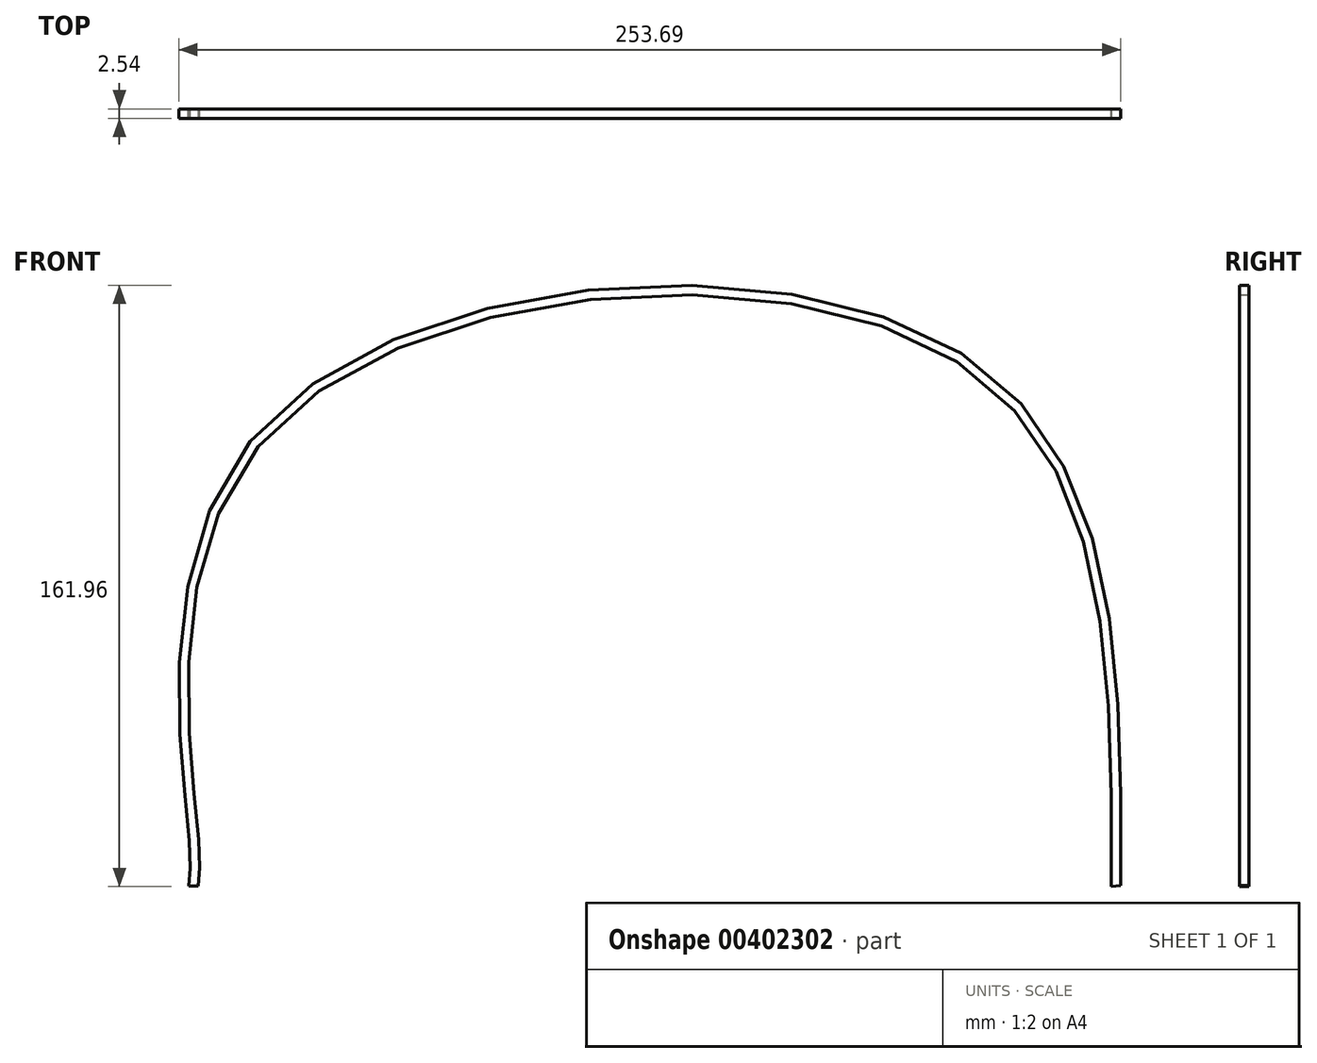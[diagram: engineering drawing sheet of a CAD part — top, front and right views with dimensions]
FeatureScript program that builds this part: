
annotation { "Feature Type Name" : "Feature", "Feature Type Description" : "" }
export const myFeature = defineFeature(function(context is Context, id is Id, definition is map)
    precondition{}
    {
        {
            var Q0;
            Q0=qCreatedBy(makeId("Top.planeOp"),FACE);
            var sketch = newSketch(context, id + "F0", { "sketchPlane" : qUnion([Q0])});
            skLineSegment(sketch, "E0.bottom", {"start": v(-1.27, 1.27) * mm, "end": v(1.27, 1.27) * mm});
            skLineSegment(sketch, "E0.top", {"start": v(-1.27, -1.27) * mm, "end": v(1.27, -1.27) * mm});
            skLineSegment(sketch, "E0.left", {"start": v(-1.27, 1.27) * mm, "end": v(-1.27, -1.27) * mm});
            skLineSegment(sketch, "E0.right", {"start": v(1.27, 1.27) * mm, "end": v(1.27, -1.27) * mm});
            skPoint(sketch, "E0.middle", {"position": v(0, 0) * mm});
            skSolve(sketch);
        }
        {
            var Q0;
            Q0=qCreatedBy(makeId("Front.planeOp"),FACE);
            var sketch = newSketch(context, id + "F1", { "sketchPlane" : qUnion([Q0])});
            skFitSpline(sketch, "E1", {"points": [v(0, 0) * mm, v(0, 13.6) * mm, v(17.69, 120.67) * mm, v(206.35, 142.35) * mm, v(248.42, 0) * mm], "startDerivative": vector(9.9, 103.05) * mm, "endDerivative": vector(-2.5, -568.63) * mm});
            skSolve(sketch);
        }
        {
            var Q0;
            Q0 = qSketchRegion(id + "F0", true);
            var Q1;
            Q1 = qConstructionFilter(qBodyType(qCreatedBy(id + "F1" ,EDGE), BodyType.WIRE), ConstructionObject.NO);
            sweep(context, id + "F2", {"profiles" : qUnion([Q0]), "path" : qUnion([Q1])});
        }
    });
